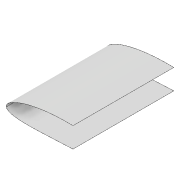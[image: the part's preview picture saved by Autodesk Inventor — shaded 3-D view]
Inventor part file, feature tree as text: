
AUTODESK INVENTOR PART (.ipt)
format: ipt  version: 2022 (Build 260153000, 153)  size: 427,008 bytes
history: native  units: mm
features: extrude x14, sketch x12, projected_geometry x9, plane x4, thicken_offset x1, shell x1, fillet x1
ambient origin geometry x8: Origin, YZ Plane, XZ Plane, XY Plane, X Axis, Y Axis, Z Axis, Center Point
bodies: Solid1 (feature_tree)
feature tree (42):
  extrude  "Extrusion1"  Depth=0.2mm
  thicken_offset  "Thicken1"
  shell  "Shell1"  Thickness=5.215mm
  extrude  "Extrusion23"  Depth=63.6mm
  plane  "Work Plane3"
  sketch  "Sketch26"  dims[d69=4.1mm d70=63.6mm]
  plane  "Work Plane4"
  extrude  "Extrusion9"  Depth=4.2mm
  plane  "Work Plane5"
  sketch  "Sketch38"  dims[d88=2.0mm d89=4.0mm]
  extrude  "Extrusion10"  Depth=6.0mm
  extrude  "Extrusion11"  Depth=21.0mm TaperAngle=0.0deg
  extrude  "Extrusion12"  Depth=5.0mm
  plane  "Work Plane6"
  extrude  "Extrusion13"  Depth=3.0mm TaperAngle=0.0deg
  extrude  "Extrusion15"  Depth=2.0mm
  extrude  "Extrusion16"  Depth=4.0mm
  extrude  "Extrusion17"  Depth=3.0mm TaperAngle=0.0deg
  extrude  "Extrusion20"  Depth=6.5mm TaperAngle=0.0deg
  fillet  "Fillet2"  Radius=28.0mm
  extrude  "Extrusion18"  Depth=200.0mm
  extrude  "Extrusion21"  Depth=100.0mm TaperAngle=0.0deg
  extrude  "Extrusion22"  Depth=7.0mm
  sketch  "Sketch3"  dims[d0=300.0mm d1=0.0mm d2=0.2mm d68=5.215mm]
  sketch  "Sketch27"  dims[d71=16.0mm d72=4.2mm]
  projected_geometry  "Projected Loop13"
  sketch  "Sketch29"  dims[d73=63.6mm d74=6.0mm]
  sketch  "Sketch30"  dims[d75=7.0mm d76=21.0mm d77=0.0mm]
  projected_geometry  "Projected Loop14"
  sketch  "Sketch31"  dims[d78=-11.0mm d79=5.0mm]
  projected_geometry  "Projected Loop15"
  projected_geometry  "Projected Loop16"
  projected_geometry  "Projected Loop17"
  sketch  "Sketch33"  dims[d80=10.0mm d83=3.0mm d84=0.0mm]
  projected_geometry  "Projected Loop18"
  projected_geometry  "Projected Loop19"
  sketch  "Sketch36"  dims[d86=0.65mm d87=2.0mm]
  projected_geometry  "Projected Loop20"
  sketch  "Sketch39"  dims[d90=4.0mm d91=3.0mm d92=0.0mm]
  sketch  "Sketch41"  dims[d93=12.0mm d94=6.5mm d95=0.0mm d96=28.0mm]
  sketch  "Sketch42"  dims[d98=9.0mm d99=0.0mm d103=200.0mm d104=100.0mm d105=0.0mm d106=7.0mm d107=4.1mm d108=7.0mm d109=2.0mm d110=0.0mm d111=2.0mm d112=0.0mm d113=2.0mm d114=95.0mm d115=10.0mm d116=0.0mm d119=100.0mm d120=0.0mm d121=1.0mm d122=3.0mm d123=0.0mm d124=10.0mm d125=0.0mm d126=0.2mm d127=1.0mm d128=200.0mm d129=1000.0mm d130=0.0mm]
  projected_geometry  "Project Cut Edges1"
